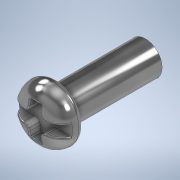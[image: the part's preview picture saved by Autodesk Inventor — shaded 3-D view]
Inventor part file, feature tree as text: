
AUTODESK INVENTOR PART (.ipt)
format: ipt  version: 2021 (Build 250183000, 183)  size: 309,760 bytes
history: native  units: mm
features: fillet x5, sketch x4, extrude x3, other x1, revolve x1
ambient origin geometry x8: Origin, YZ Plane, XZ Plane, XY Plane, X Axis, Y Axis, Z Axis, Center Point
bodies: Body1 (feature_tree)
feature tree (14):
  other  "ソリッド1"
  extrude  "押し出し1"  Depth=3.0mm
  revolve  "回転1"
  fillet  "フィレット1"  Radius=8.0mm
  fillet  "フィレット2"  Radius=2.5mm
  extrude  "押し出し2"  Depth=2.5mm
  extrude  "押し出し3"  Depth=5.0mm
  fillet  "フィレット3"  Radius=2.0mm
  fillet  "フィレット4"  [1 undecoded]
  fillet  "フィレット5"  Radius=0.5mm
  sketch  "スケッチ1"
  sketch  "スケッチ2"
  sketch  "スケッチ3"
  sketch  "スケッチ4"
note: 1 required parameter value undecoded (feature->parameter linkage not recoverable at this tier; creation-order binding heuristic only, values carry confidence <= 0.55)
